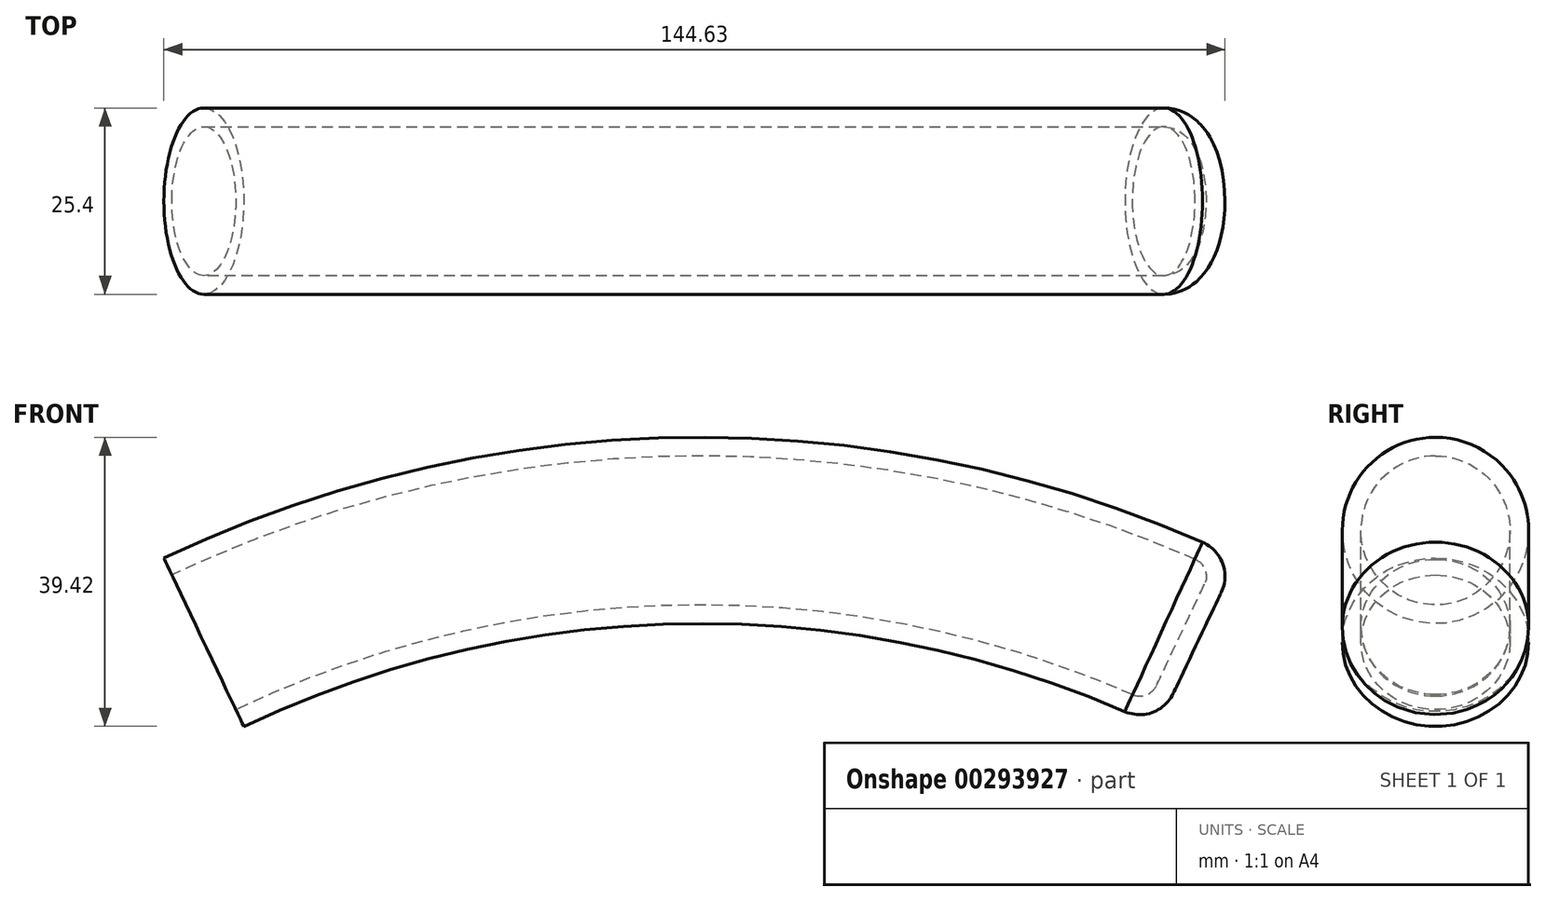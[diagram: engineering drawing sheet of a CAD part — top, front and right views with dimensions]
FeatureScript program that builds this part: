
annotation { "Feature Type Name" : "Feature", "Feature Type Description" : "" }
export const myFeature = defineFeature(function(context is Context, id is Id, definition is map)
    precondition{}
    {
        {
            var Q0;
            Q0=qCreatedBy(makeId("Front.planeOp"),FACE);
            var sketch = newSketch(context, id + "F0", { "sketchPlane" : qUnion([Q0])});
            skArc(sketch, "E0", {"start": v(62.06, 0) * mm, "mid": v(-5.67, 15.25) * mm, "end": v(-73.4, 0) * mm});
            skSolve(sketch);
        }
        {
            var Q0;
            Q0=sQuery(id+"F0.wireOp",EDGE,"E0");
            var Q1;
            Q1=sQuery(id+"F0.wireOp",VERTEX,"E0.start");
            cPlane(context, id + "F1", {"entities" : qUnion([Q0, Q1]), "cplaneType" : CPlaneType.CURVE_POINT, "offset" : 25.4 * mm, "width" : 152.4 * mm, "height" : 152.4 * mm});
        }
        {
            var Q0;
            Q0=qCreatedBy(id+"F1.planeOp",FACE);
            var sketch = newSketch(context, id + "F2", { "sketchPlane" : qUnion([Q0])});
            skCircle(sketch, "E1", {"center": v(0, 26.6) * mm, "radius": 12.7 * mm});
            skSolve(sketch);
        }
        {
            var Q0;
            Q0=makeQuery(id+"F2.imprint","IMPRINT",FACE,{"disambiguationData":[TD([[makeQuery(id+"F2.imprint","IMPRINT",EDGE,{"derivedFrom":sQuery(id+"F2.wireOp",EDGE,"E1")}),1.0]])]});
            var Q1;
            Q1=sQuery(id+"F0.wireOp",EDGE,"E0");
            sweep(context, id + "F3", {"profiles" : qUnion([Q0]), "path" : qUnion([Q1])});
        }
        {
            var Q0;
            Q0=makeQuery(id+"F3.opSweep","CAP_EDGE",EDGE,{"disambiguationData":[OSD([sQuery(id+"F0.wireOp",VERTEX,"E0.start"),sQuery(id+"F2.wireOp",EDGE,"E1")])],"isStart":true});
            fillet(context, id + "F4", {"entities" : qUnion([Q0]), "radius" : 5.08 * mm, "tangentPropagation" : true, "allowEdgeOverflow" : false});
        }
        {
            var Q0;
            Q0=makeQuery(id+"F3.opSweep","CAP_FACE",FACE,{"disambiguationData":[OSD([sQuery(id+"F0.wireOp",VERTEX,"E0.end"),sQuery(id+"F2.wireOp",EDGE,"E1")])],"isStart":false});
            shell(context, id + "F5", {"entities" : qUnion([Q0]), "thickness" : 2.54 * mm});
        }
    });
